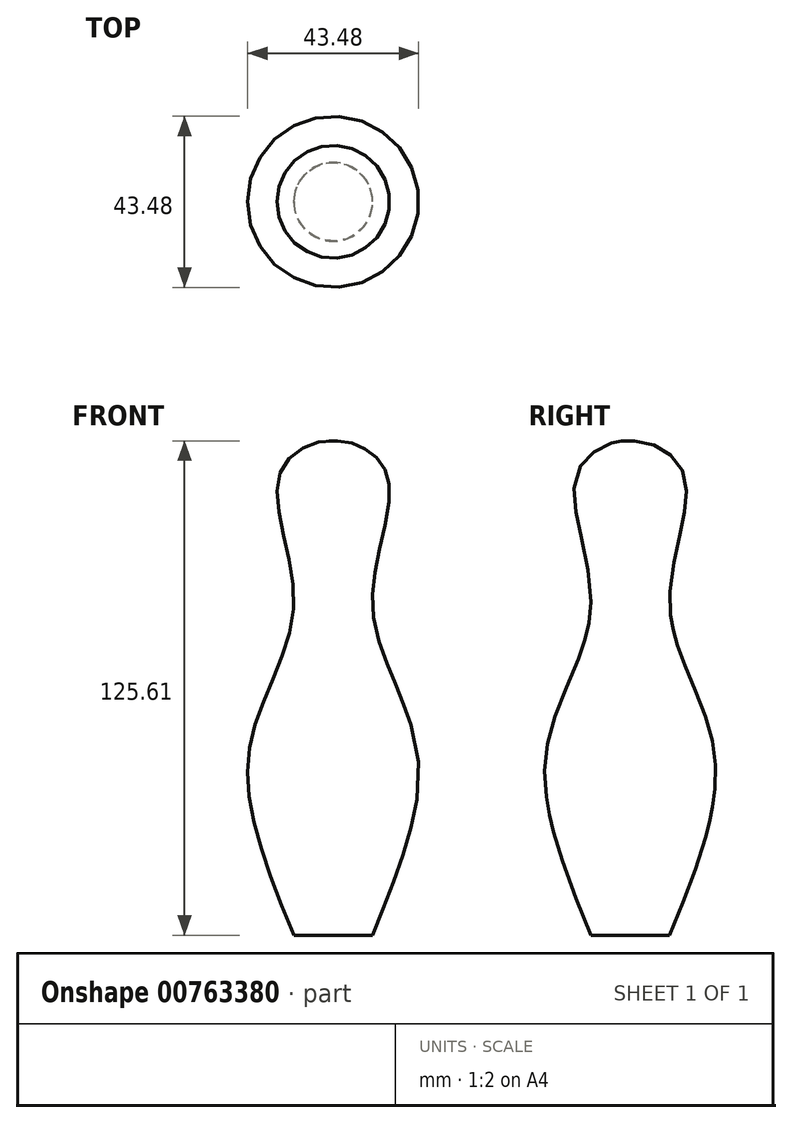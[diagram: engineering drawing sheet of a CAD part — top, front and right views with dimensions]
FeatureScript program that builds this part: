
annotation { "Feature Type Name" : "Feature", "Feature Type Description" : "" }
export const myFeature = defineFeature(function(context is Context, id is Id, definition is map)
    precondition{}
    {
        {
            var Q0;
            Q0=qCreatedBy(makeId("Front.planeOp"),FACE);
            var sketch = newSketch(context, id + "F0", { "sketchPlane" : qUnion([Q0])});
            skLineSegment(sketch, "E0", {"start": v(0, 0) * mm, "end": v(0, 125.55) * mm, "construction": true});
            skLineSegment(sketch, "E1", {"start": v(0, 0) * mm, "end": v(-10, 0) * mm});
            skFitSpline(sketch, "E2", {"points": [v(-10, 0) * mm, v(-21.23, 47.72) * mm, v(-10, 84.21) * mm, v(-13.5, 117.54) * mm, v(0, 125.55) * mm], "startDerivative": vector(-72.9, 179.9) * mm, "endDerivative": vector(79.11, -9.72) * mm});
            skLineSegment(sketch, "E3", {"start": v(0, 125.55) * mm, "end": v(0, 0) * mm});
            skSolve(sketch);
        }
        {
            var Q0;
            Q0=makeQuery(id+"F0.imprint","IMPRINT",FACE,{"disambiguationData":[TD([[makeQuery(id+"F0.imprint","IMPRINT",EDGE,{"derivedFrom":sQuery(id+"F0.wireOp",EDGE,"E1")}),-1.0]])]});
            var Q1;
            Q1=sQuery(id+"F0.wireOp",EDGE,"E3");
            revolve(context, id + "F1", {"surfaceOperationType" : NewSurfaceOperationType.NEW, "entities" : qUnion([Q0]), "axis" : qUnion([Q1]), "revolveType" : RevolveType.FULL});
        }
    });
